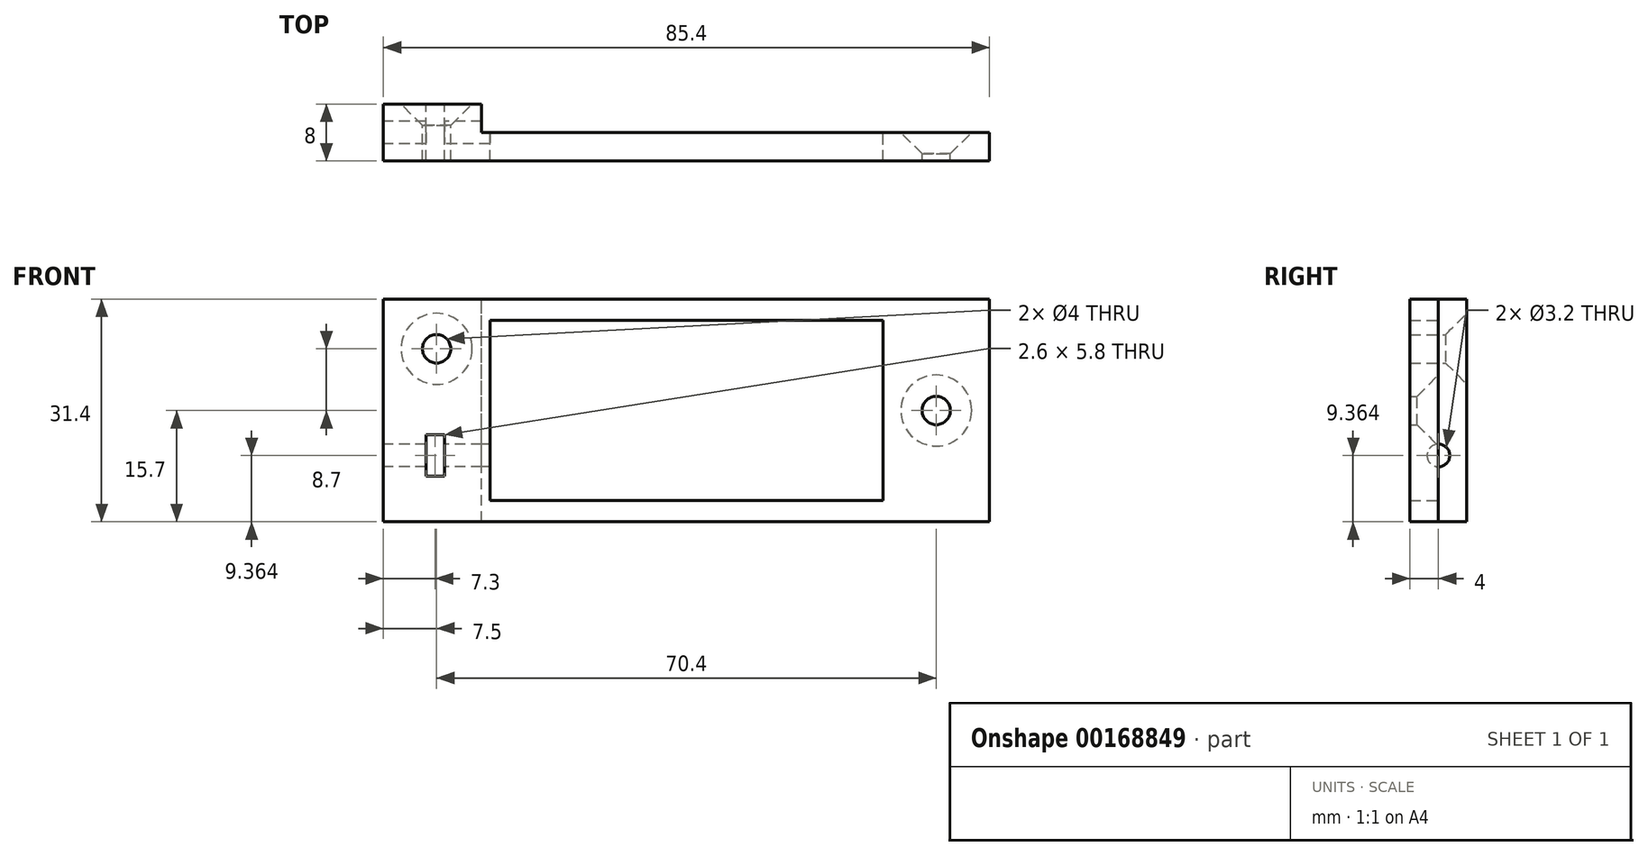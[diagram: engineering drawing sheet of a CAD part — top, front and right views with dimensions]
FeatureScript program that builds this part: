
annotation { "Feature Type Name" : "Feature", "Feature Type Description" : "" }
export const myFeature = defineFeature(function(context is Context, id is Id, definition is map)
    precondition{}
    {
        {
            var Q0;
            Q0=qCreatedBy(makeId("Front.planeOp"),FACE);
            var sketch = newSketch(context, id + "F0", { "sketchPlane" : qUnion([Q0])});
            skLineSegment(sketch, "E0.bottom", {"start": v(27.7, -12.7) * mm, "end": v(-27.7, -12.7) * mm});
            skLineSegment(sketch, "E0.top", {"start": v(27.7, 12.7) * mm, "end": v(-27.7, 12.7) * mm});
            skLineSegment(sketch, "E0.left", {"start": v(27.7, -12.7) * mm, "end": v(27.7, 12.7) * mm});
            skLineSegment(sketch, "E0.right", {"start": v(-27.7, -12.7) * mm, "end": v(-27.7, 12.7) * mm});
            skPoint(sketch, "E0.middle", {"position": v(0, 0) * mm});
            skLineSegment(sketch, "E1.bottom", {"start": v(42.7, -15.7) * mm, "end": v(-42.7, -15.7) * mm});
            skLineSegment(sketch, "E1.top", {"start": v(42.7, 15.7) * mm, "end": v(-42.7, 15.7) * mm});
            skLineSegment(sketch, "E1.left", {"start": v(42.7, -15.7) * mm, "end": v(42.7, 15.7) * mm});
            skLineSegment(sketch, "E1.right", {"start": v(-42.7, -15.7) * mm, "end": v(-42.7, 15.7) * mm});
            skCircle(sketch, "E2", {"center": v(35.2, 0) * mm, "radius": 2 * mm});
            skPoint(sketch, "E2.centerSnap0", {"position": v(42.7, 0) * mm});
            skCircle(sketch, "E3", {"center": v(-35.2, 8.7) * mm, "radius": 2 * mm});
            skLineSegment(sketch, "E4.bottom", {"start": v(-36.7, -3.44) * mm, "end": v(-34.1, -3.44) * mm});
            skLineSegment(sketch, "E4.top", {"start": v(-36.7, -9.24) * mm, "end": v(-34.1, -9.24) * mm});
            skLineSegment(sketch, "E4.left", {"start": v(-36.7, -3.44) * mm, "end": v(-36.7, -9.24) * mm});
            skLineSegment(sketch, "E4.right", {"start": v(-34.1, -3.44) * mm, "end": v(-34.1, -9.24) * mm});
            skPoint(sketch, "E4.middle", {"position": v(-35.4, -6.34) * mm});
            skSolve(sketch);
        }
        {
            var Q0;
            Q0=makeQuery(id+"F0.imprint","IMPRINT",FACE,{"disambiguationData":[TD([[makeQuery(id+"F0.imprint","IMPRINT",EDGE,{"derivedFrom":sQuery(id+"F0.wireOp",EDGE,"E0.bottom")}),1.0]])]});
            extrude(context, id + "F1", {"entities" : qUnion([Q0]), "depth" : 4 * mm});
        }
        {
            var Q0;
            Q0=makeQuery(id+"F1.opExtrude","CAP_FACE",FACE,{"disambiguationData":[OSD([sQuery(id+"F0.wireOp",EDGE,"E0.bottom"),sQuery(id+"F0.wireOp",EDGE,"E0.top"),sQuery(id+"F0.wireOp",EDGE,"E0.left"),sQuery(id+"F0.wireOp",EDGE,"E0.right"),sQuery(id+"F0.wireOp",EDGE,"E1.bottom"),sQuery(id+"F0.wireOp",EDGE,"E1.top"),sQuery(id+"F0.wireOp",EDGE,"E1.left"),sQuery(id+"F0.wireOp",EDGE,"E1.right"),sQuery(id+"F0.wireOp",EDGE,"E2"),sQuery(id+"F0.wireOp",EDGE,"E3"),sQuery(id+"F0.wireOp",EDGE,"E4.bottom"),sQuery(id+"F0.wireOp",EDGE,"E4.top"),sQuery(id+"F0.wireOp",EDGE,"E4.left"),sQuery(id+"F0.wireOp",EDGE,"E4.right")])],"isStart":true});
            var sketch = newSketch(context, id + "F2", { "sketchPlane" : qUnion([Q0])});
            skLineSegment(sketch, "E5.0", {"start": v(42.7, -15.7) * mm, "end": v(42.7, 15.7) * mm, "construction": true});
            skLineSegment(sketch, "E6.bottom", {"start": v(42.7, -15.7) * mm, "end": v(28.85, -15.7) * mm});
            skLineSegment(sketch, "E6.top", {"start": v(42.7, 15.7) * mm, "end": v(28.85, 15.7) * mm});
            skLineSegment(sketch, "E6.left", {"start": v(42.7, -15.7) * mm, "end": v(42.7, 15.7) * mm});
            skLineSegment(sketch, "E6.right", {"start": v(28.85, -15.7) * mm, "end": v(28.85, 15.7) * mm});
            skLineSegment(sketch, "E7.0", {"start": v(36.7, -9.24) * mm, "end": v(34.1, -9.24) * mm});
            skLineSegment(sketch, "E7.1", {"start": v(34.1, -3.44) * mm, "end": v(34.1, -9.24) * mm});
            skLineSegment(sketch, "E7.3", {"start": v(36.7, -3.44) * mm, "end": v(36.7, -9.24) * mm});
            skLineSegment(sketch, "E7.4", {"start": v(36.7, -3.44) * mm, "end": v(34.1, -3.44) * mm});
            skLineSegment(sketch, "E7.8", {"start": v(34.1, -3.44) * mm, "end": v(34.1, -9.24) * mm});
            skLineSegment(sketch, "E7.9", {"start": v(36.7, -9.24) * mm, "end": v(34.1, -9.24) * mm});
            skLineSegment(sketch, "E7.10", {"start": v(36.7, -3.44) * mm, "end": v(36.7, -9.24) * mm});
            skLineSegment(sketch, "E7.11", {"start": v(36.7, -3.44) * mm, "end": v(34.1, -3.44) * mm});
            skCircle(sketch, "E8.0", {"center": v(35.2, 8.7) * mm, "radius": 2 * mm});
            skSolve(sketch);
        }
        {
            var Q0;
            Q0 = qSketchRegion(id + "F2", true);
            extrude(context, id + "F3", {"entities" : qUnion([Q0]), "operationType" : NewBodyOperationType.ADD, "depth" : 4 * mm});
        }
        {
            var Q0;
            Q0=makeQuery(id+"F1.opExtrude","SWEPT_FACE",FACE,{"disambiguationData":[OSD([sQuery(id+"F0.wireOp",EDGE,"E1.right")])]});
            var sketch = newSketch(context, id + "F4", { "sketchPlane" : qUnion([Q0])});
            skLineSegment(sketch, "E9.0", {"start": v(0, -3.44) * mm, "end": v(0, -9.24) * mm, "construction": true});
            skLineSegment(sketch, "E10", {"start": v(0, -6.34) * mm, "end": v(4, -6.34) * mm, "construction": true});
            skCircle(sketch, "E11", {"center": v(0, -6.34) * mm, "radius": 1.6 * mm});
            skSolve(sketch);
        }
        {
            var Q0;
            Q0 = qSketchRegion(id + "F4", true);
            extrude(context, id + "F5", {"entities" : qUnion([Q0]), "operationType" : NewBodyOperationType.REMOVE, "oppositeDirection" : true, "depth" : 25 * mm});
        }
        {
            var Q0;
            Q0=makeQuery(id+"F3.opExtrude","CAP_EDGE",EDGE,{"disambiguationData":[OSD([sQuery(id+"F2.wireOp",EDGE,"E8.0")])],"isStart":false});
            var Q1;
            Q1=makeQuery(id+"F1.opExtrude","CAP_EDGE",EDGE,{"disambiguationData":[OSD([sQuery(id+"F0.wireOp",EDGE,"E2")])],"isStart":true});
            chamfer(context, id + "F6", {"entities" : qUnion([Q0, Q1]), "width" : 3 * mm, "tangentPropagation" : true});
        }
    });
